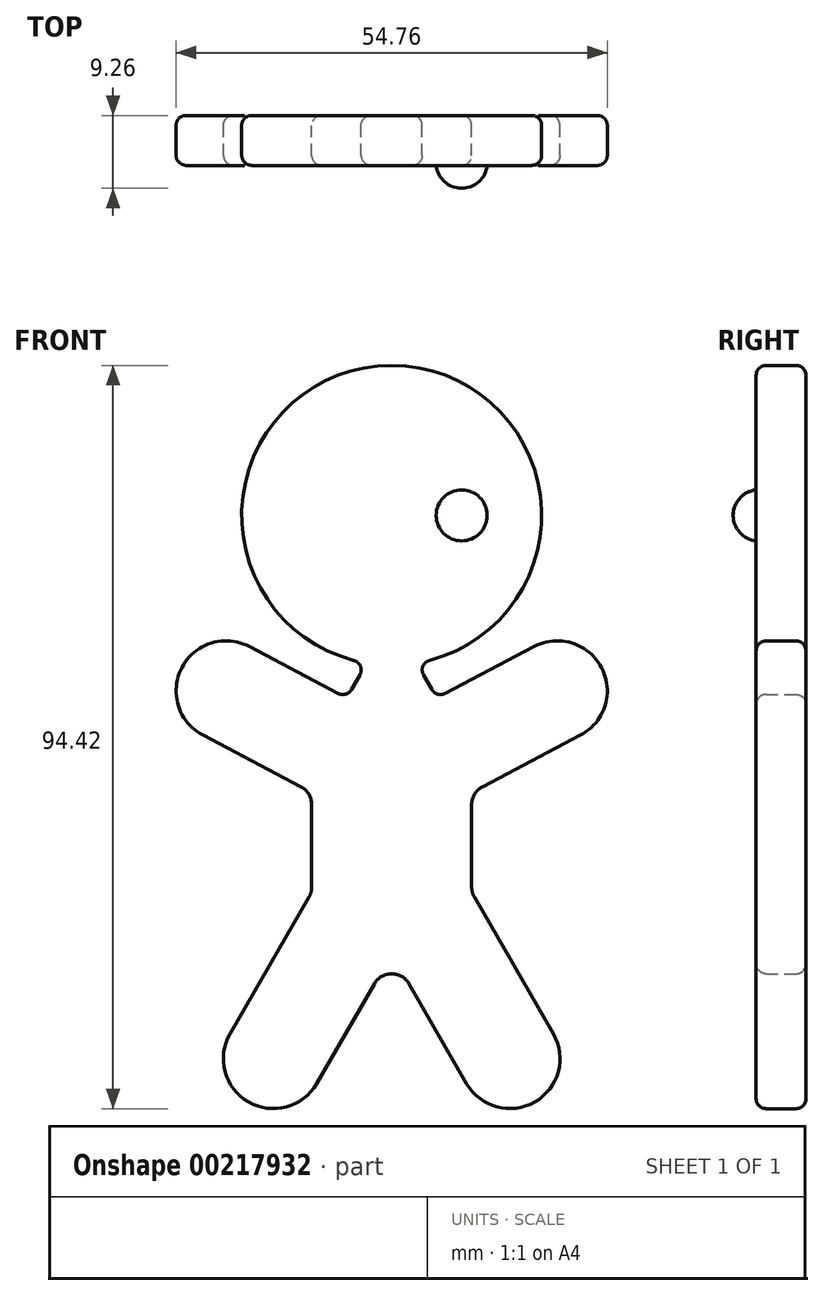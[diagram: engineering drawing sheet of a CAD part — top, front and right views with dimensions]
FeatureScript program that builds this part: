
annotation { "Feature Type Name" : "Feature", "Feature Type Description" : "" }
export const myFeature = defineFeature(function(context is Context, id is Id, definition is map)
    precondition{}
    {
        {
            var Q0;
            Q0=qCreatedBy(makeId("Front.planeOp"),FACE);
            var sketch = newSketch(context, id + "F0", { "sketchPlane" : qUnion([Q0])});
            skArc(sketch, "E0", {"start": v(4.82, 59.27) * mm, "mid": v(0, 96.74) * mm, "end": v(-4.82, 59.27) * mm});
            skLineSegment(sketch, "E1", {"start": v(2.2, 18.19) * mm, "end": v(9.52, 5.5) * mm});
            skLineSegment(sketch, "E2", {"start": v(18.2, 3.18) * mm, "end": v(18.2, 3.18) * mm});
            skLineSegment(sketch, "E3", {"start": v(20.52, 11.85) * mm, "end": v(10.5, 29.21) * mm});
            skLineSegment(sketch, "E4", {"start": v(10.16, 30.48) * mm, "end": v(10.16, 40.97) * mm});
            skLineSegment(sketch, "E5", {"start": v(11.52, 43.21) * mm, "end": v(24, 49.78) * mm});
            skLineSegment(sketch, "E6", {"start": v(26.65, 58.35) * mm, "end": v(26.65, 58.35) * mm});
            skLineSegment(sketch, "E7", {"start": v(18.08, 61.02) * mm, "end": v(6.8, 55.08) * mm});
            skLineSegment(sketch, "E8", {"start": v(0, 77.7) * mm, "end": v(0, 22) * mm, "construction": true});
            skLineSegment(sketch, "E9", {"start": v(5.1, 55.57) * mm, "end": v(4.05, 57.4) * mm});
            skLineSegment(sketch, "E10.MirrorCS", {"start": v(-2.2, 18.19) * mm, "end": v(-9.52, 5.5) * mm});
            skLineSegment(sketch, "E11.MirrorCS", {"start": v(-18.2, 3.17) * mm, "end": v(-18.2, 3.17) * mm});
            skLineSegment(sketch, "E12.MirrorCS", {"start": v(-20.52, 11.85) * mm, "end": v(-10.5, 29.21) * mm});
            skLineSegment(sketch, "E13.MirrorCS", {"start": v(-10.16, 30.48) * mm, "end": v(-10.16, 40.97) * mm});
            skLineSegment(sketch, "E14.MirrorCS", {"start": v(-11.52, 43.21) * mm, "end": v(-24, 49.78) * mm});
            skLineSegment(sketch, "E15.MirrorCS", {"start": v(-26.65, 58.35) * mm, "end": v(-26.65, 58.35) * mm});
            skLineSegment(sketch, "E16.MirrorCS", {"start": v(-18.08, 61.02) * mm, "end": v(-6.8, 55.08) * mm});
            skLineSegment(sketch, "E17.MirrorCS", {"start": v(-5.1, 55.57) * mm, "end": v(-4.05, 57.4) * mm});
            skPoint(sketch, "E18.visualSharp", {"position": v(12.7, 0) * mm});
            skArc(sketch, "E18.filletArc", {"start": v(9.53, 5.5) * mm, "mid": v(13.38, 2.54) * mm, "end": v(18.2, 3.18) * mm});
            skPoint(sketch, "E19.visualSharp", {"position": v(23.7, 6.35) * mm});
            skArc(sketch, "E19.filletArc", {"start": v(18.2, 3.18) * mm, "mid": v(21.16, 7.03) * mm, "end": v(20.52, 11.85) * mm});
            skPoint(sketch, "E20.visualSharp", {"position": v(-12.7, 0) * mm});
            skArc(sketch, "E20.filletArc", {"start": v(-18.2, 3.18) * mm, "mid": v(-13.38, 2.54) * mm, "end": v(-9.52, 5.5) * mm});
            skPoint(sketch, "E21.visualSharp", {"position": v(-23.7, 6.35) * mm});
            skArc(sketch, "E21.filletArc", {"start": v(-20.52, 11.85) * mm, "mid": v(-21.16, 7.03) * mm, "end": v(-18.2, 3.17) * mm});
            skPoint(sketch, "E22.visualSharp", {"position": v(23.7, 63.97) * mm});
            skArc(sketch, "E22.filletArc", {"start": v(26.65, 58.35) * mm, "mid": v(22.92, 61.46) * mm, "end": v(18.08, 61.02) * mm});
            skPoint(sketch, "E23.visualSharp", {"position": v(29.61, 52.73) * mm});
            skArc(sketch, "E23.filletArc", {"start": v(24, 49.78) * mm, "mid": v(27.1, 53.51) * mm, "end": v(26.65, 58.35) * mm});
            skPoint(sketch, "E24.visualSharp", {"position": v(-23.7, 63.97) * mm});
            skArc(sketch, "E24.filletArc", {"start": v(-18.08, 61.02) * mm, "mid": v(-22.92, 61.46) * mm, "end": v(-26.65, 58.35) * mm});
            skPoint(sketch, "E25.visualSharp", {"position": v(-29.61, 52.73) * mm});
            skArc(sketch, "E25.filletArc", {"start": v(-26.65, 58.35) * mm, "mid": v(-27.1, 53.51) * mm, "end": v(-24, 49.78) * mm});
            skPoint(sketch, "E26.visualSharp", {"position": v(0, 22) * mm});
            skArc(sketch, "E26.filletArc", {"start": v(2.2, 18.19) * mm, "mid": v(0, 19.46) * mm, "end": v(-2.2, 18.19) * mm});
            skPoint(sketch, "E27.visualSharp", {"position": v(-10.16, 29.8) * mm});
            skArc(sketch, "E27.filletArc", {"start": v(-10.5, 29.2) * mm, "mid": v(-10.25, 29.82) * mm, "end": v(-10.16, 30.48) * mm});
            skPoint(sketch, "E28.visualSharp", {"position": v(10.16, 29.8) * mm});
            skArc(sketch, "E28.filletArc", {"start": v(10.16, 30.48) * mm, "mid": v(10.25, 29.82) * mm, "end": v(10.5, 29.2) * mm});
            skPoint(sketch, "E29.visualSharp", {"position": v(10.16, 42.5) * mm});
            skArc(sketch, "E29.filletArc", {"start": v(11.52, 43.21) * mm, "mid": v(10.53, 42.28) * mm, "end": v(10.16, 40.97) * mm});
            skPoint(sketch, "E30.visualSharp", {"position": v(-10.16, 42.5) * mm});
            skArc(sketch, "E30.filletArc", {"start": v(-10.16, 40.97) * mm, "mid": v(-10.53, 42.28) * mm, "end": v(-11.52, 43.21) * mm});
            skPoint(sketch, "E31.visualSharp", {"position": v(-5.72, 54.51) * mm});
            skArc(sketch, "E31.filletArc", {"start": v(-6.8, 55.08) * mm, "mid": v(-5.85, 54.98) * mm, "end": v(-5.1, 55.57) * mm});
            skPoint(sketch, "E32.visualSharp", {"position": v(5.72, 54.51) * mm});
            skArc(sketch, "E32.filletArc", {"start": v(5.1, 55.57) * mm, "mid": v(5.85, 54.98) * mm, "end": v(6.8, 55.08) * mm});
            skPoint(sketch, "E33.visualSharp", {"position": v(-3.18, 58.91) * mm});
            skArc(sketch, "E33.filletArc", {"start": v(-4.05, 57.4) * mm, "mid": v(-3.97, 58.53) * mm, "end": v(-4.82, 59.27) * mm});
            skPoint(sketch, "E34.visualSharp", {"position": v(3.18, 58.91) * mm});
            skArc(sketch, "E34.filletArc", {"start": v(4.82, 59.27) * mm, "mid": v(3.97, 58.53) * mm, "end": v(4.05, 57.4) * mm});
            skSolve(sketch);
        }
        {
            var Q0;
            Q0 = qSketchRegion(id + "F0", true);
            extrude(context, id + "F1", {"entities" : qUnion([Q0]), "depth" : 6.35 * mm});
        }
        {
            var Q0;
            Q0=makeQuery(id+"F1.opExtrude","CAP_FACE",FACE,{"disambiguationData":[OSD([sQuery(id+"F0.wireOp",EDGE,"E0"),sQuery(id+"F0.wireOp",EDGE,"E1"),sQuery(id+"F0.wireOp",EDGE,"E3"),sQuery(id+"F0.wireOp",EDGE,"E4"),sQuery(id+"F0.wireOp",EDGE,"E5"),sQuery(id+"F0.wireOp",EDGE,"E7"),sQuery(id+"F0.wireOp",EDGE,"E9"),sQuery(id+"F0.wireOp",EDGE,"E10.MirrorCS"),sQuery(id+"F0.wireOp",EDGE,"E12.MirrorCS"),sQuery(id+"F0.wireOp",EDGE,"E13.MirrorCS"),sQuery(id+"F0.wireOp",EDGE,"E14.MirrorCS"),sQuery(id+"F0.wireOp",EDGE,"E16.MirrorCS"),sQuery(id+"F0.wireOp",EDGE,"E17.MirrorCS"),sQuery(id+"F0.wireOp",EDGE,"E18.filletArc"),sQuery(id+"F0.wireOp",EDGE,"E19.filletArc"),sQuery(id+"F0.wireOp",EDGE,"E20.filletArc"),sQuery(id+"F0.wireOp",EDGE,"E21.filletArc"),sQuery(id+"F0.wireOp",EDGE,"E22.filletArc"),sQuery(id+"F0.wireOp",EDGE,"E23.filletArc"),sQuery(id+"F0.wireOp",EDGE,"E24.filletArc"),sQuery(id+"F0.wireOp",EDGE,"E25.filletArc"),sQuery(id+"F0.wireOp",EDGE,"E26.filletArc"),sQuery(id+"F0.wireOp",EDGE,"E27.filletArc"),sQuery(id+"F0.wireOp",EDGE,"E28.filletArc"),sQuery(id+"F0.wireOp",EDGE,"E29.filletArc"),sQuery(id+"F0.wireOp",EDGE,"E30.filletArc"),sQuery(id+"F0.wireOp",EDGE,"E31.filletArc"),sQuery(id+"F0.wireOp",EDGE,"E32.filletArc"),sQuery(id+"F0.wireOp",EDGE,"E33.filletArc"),sQuery(id+"F0.wireOp",EDGE,"E34.filletArc")])],"isStart":false});
            var Q1;
            Q1=makeQuery(id+"F1.opExtrude","CAP_FACE",FACE,{"disambiguationData":[OSD([sQuery(id+"F0.wireOp",EDGE,"E0"),sQuery(id+"F0.wireOp",EDGE,"E1"),sQuery(id+"F0.wireOp",EDGE,"E3"),sQuery(id+"F0.wireOp",EDGE,"E4"),sQuery(id+"F0.wireOp",EDGE,"E5"),sQuery(id+"F0.wireOp",EDGE,"E7"),sQuery(id+"F0.wireOp",EDGE,"E9"),sQuery(id+"F0.wireOp",EDGE,"E10.MirrorCS"),sQuery(id+"F0.wireOp",EDGE,"E12.MirrorCS"),sQuery(id+"F0.wireOp",EDGE,"E13.MirrorCS"),sQuery(id+"F0.wireOp",EDGE,"E14.MirrorCS"),sQuery(id+"F0.wireOp",EDGE,"E16.MirrorCS"),sQuery(id+"F0.wireOp",EDGE,"E17.MirrorCS"),sQuery(id+"F0.wireOp",EDGE,"E18.filletArc"),sQuery(id+"F0.wireOp",EDGE,"E19.filletArc"),sQuery(id+"F0.wireOp",EDGE,"E20.filletArc"),sQuery(id+"F0.wireOp",EDGE,"E21.filletArc"),sQuery(id+"F0.wireOp",EDGE,"E22.filletArc"),sQuery(id+"F0.wireOp",EDGE,"E23.filletArc"),sQuery(id+"F0.wireOp",EDGE,"E24.filletArc"),sQuery(id+"F0.wireOp",EDGE,"E25.filletArc"),sQuery(id+"F0.wireOp",EDGE,"E26.filletArc"),sQuery(id+"F0.wireOp",EDGE,"E27.filletArc"),sQuery(id+"F0.wireOp",EDGE,"E28.filletArc"),sQuery(id+"F0.wireOp",EDGE,"E29.filletArc"),sQuery(id+"F0.wireOp",EDGE,"E30.filletArc"),sQuery(id+"F0.wireOp",EDGE,"E31.filletArc"),sQuery(id+"F0.wireOp",EDGE,"E32.filletArc"),sQuery(id+"F0.wireOp",EDGE,"E33.filletArc"),sQuery(id+"F0.wireOp",EDGE,"E34.filletArc")])],"isStart":true});
            fillet(context, id + "F2", {"entities" : qUnion([Q0, Q1]), "radius" : 1.27 * mm, "tangentPropagation" : true, "allowEdgeOverflow" : false});
        }
        {
            var Q0;
            Q0=makeQuery(id+"F1.opExtrude","CAP_FACE",FACE,{"disambiguationData":[OSD([sQuery(id+"F0.wireOp",EDGE,"E0"),sQuery(id+"F0.wireOp",EDGE,"E1"),sQuery(id+"F0.wireOp",EDGE,"E3"),sQuery(id+"F0.wireOp",EDGE,"E4"),sQuery(id+"F0.wireOp",EDGE,"E5"),sQuery(id+"F0.wireOp",EDGE,"E7"),sQuery(id+"F0.wireOp",EDGE,"E9"),sQuery(id+"F0.wireOp",EDGE,"E10.MirrorCS"),sQuery(id+"F0.wireOp",EDGE,"E12.MirrorCS"),sQuery(id+"F0.wireOp",EDGE,"E13.MirrorCS"),sQuery(id+"F0.wireOp",EDGE,"E14.MirrorCS"),sQuery(id+"F0.wireOp",EDGE,"E16.MirrorCS"),sQuery(id+"F0.wireOp",EDGE,"E17.MirrorCS"),sQuery(id+"F0.wireOp",EDGE,"E18.filletArc"),sQuery(id+"F0.wireOp",EDGE,"E19.filletArc"),sQuery(id+"F0.wireOp",EDGE,"E20.filletArc"),sQuery(id+"F0.wireOp",EDGE,"E21.filletArc"),sQuery(id+"F0.wireOp",EDGE,"E22.filletArc"),sQuery(id+"F0.wireOp",EDGE,"E23.filletArc"),sQuery(id+"F0.wireOp",EDGE,"E24.filletArc"),sQuery(id+"F0.wireOp",EDGE,"E25.filletArc"),sQuery(id+"F0.wireOp",EDGE,"E26.filletArc"),sQuery(id+"F0.wireOp",EDGE,"E27.filletArc"),sQuery(id+"F0.wireOp",EDGE,"E28.filletArc"),sQuery(id+"F0.wireOp",EDGE,"E29.filletArc"),sQuery(id+"F0.wireOp",EDGE,"E30.filletArc"),sQuery(id+"F0.wireOp",EDGE,"E31.filletArc"),sQuery(id+"F0.wireOp",EDGE,"E32.filletArc"),sQuery(id+"F0.wireOp",EDGE,"E33.filletArc"),sQuery(id+"F0.wireOp",EDGE,"E34.filletArc")])],"isStart":false});
            var sketch = newSketch(context, id + "F3", { "sketchPlane" : qUnion([Q0])});
            skArc(sketch, "E35", {"start": v(8.9, 73.88) * mm, "mid": v(12.7, 77.7) * mm, "end": v(8.9, 81.5) * mm});
            skLineSegment(sketch, "E36", {"start": v(0, 95.47) * mm, "end": v(0, 20.73) * mm, "construction": true});
            skLineSegment(sketch, "E37", {"start": v(8.9, 81.5) * mm, "end": v(8.9, 73.88) * mm, "construction": true});
            skLineSegment(sketch, "E38", {"start": v(8.9, 81.5) * mm, "end": v(8.9, 73.88) * mm});
            skSolve(sketch);
        }
        {
            var Q0;
            Q0=makeQuery(id+"F1.opExtrude","CAP_FACE",FACE,{"disambiguationData":[OSD([sQuery(id+"F0.wireOp",EDGE,"E0"),sQuery(id+"F0.wireOp",EDGE,"E1"),sQuery(id+"F0.wireOp",EDGE,"E3"),sQuery(id+"F0.wireOp",EDGE,"E4"),sQuery(id+"F0.wireOp",EDGE,"E5"),sQuery(id+"F0.wireOp",EDGE,"E7"),sQuery(id+"F0.wireOp",EDGE,"E9"),sQuery(id+"F0.wireOp",EDGE,"E10.MirrorCS"),sQuery(id+"F0.wireOp",EDGE,"E12.MirrorCS"),sQuery(id+"F0.wireOp",EDGE,"E13.MirrorCS"),sQuery(id+"F0.wireOp",EDGE,"E14.MirrorCS"),sQuery(id+"F0.wireOp",EDGE,"E16.MirrorCS"),sQuery(id+"F0.wireOp",EDGE,"E17.MirrorCS"),sQuery(id+"F0.wireOp",EDGE,"E18.filletArc"),sQuery(id+"F0.wireOp",EDGE,"E19.filletArc"),sQuery(id+"F0.wireOp",EDGE,"E20.filletArc"),sQuery(id+"F0.wireOp",EDGE,"E21.filletArc"),sQuery(id+"F0.wireOp",EDGE,"E22.filletArc"),sQuery(id+"F0.wireOp",EDGE,"E23.filletArc"),sQuery(id+"F0.wireOp",EDGE,"E24.filletArc"),sQuery(id+"F0.wireOp",EDGE,"E25.filletArc"),sQuery(id+"F0.wireOp",EDGE,"E26.filletArc"),sQuery(id+"F0.wireOp",EDGE,"E27.filletArc"),sQuery(id+"F0.wireOp",EDGE,"E28.filletArc"),sQuery(id+"F0.wireOp",EDGE,"E29.filletArc"),sQuery(id+"F0.wireOp",EDGE,"E30.filletArc"),sQuery(id+"F0.wireOp",EDGE,"E31.filletArc"),sQuery(id+"F0.wireOp",EDGE,"E32.filletArc"),sQuery(id+"F0.wireOp",EDGE,"E33.filletArc"),sQuery(id+"F0.wireOp",EDGE,"E34.filletArc")])],"isStart":false});
            var sketch = newSketch(context, id + "F4", { "sketchPlane" : qUnion([Q0])});
            skLineSegment(sketch, "E39", {"start": v(0, 95.47) * mm, "end": v(0, 20.73) * mm, "construction": true});
            skFitSpline(sketch, "E40", {"points": [v(0, 68.66) * mm, v(8.71, 69.87) * mm, v(0, 64.67) * mm], "startDerivative": vector(14.82, 0.4) * mm, "endDerivative": vector(-63.33, -2.94) * mm});
            skSolve(sketch);
        }
        {
            var Q0;
            Q0=qCreatedBy(makeId("Right.planeOp"),FACE);
            var sketch = newSketch(context, id + "F5", { "sketchPlane" : qUnion([Q0])});
            skArc(sketch, "E41", {"start": v(-6.35, 69.54) * mm, "mid": v(-7.68, 68.66) * mm, "end": v(-6.35, 67.79) * mm});
            skLineSegment(sketch, "E42", {"start": v(-6.35, 69.54) * mm, "end": v(-6.35, 67.79) * mm});
            skSolve(sketch);
        }
        {
            var Q0;
            Q0=sQuery(id+"F3.wireOp",EDGE,"E38");
            cPlane(context, id + "F6", {"entities" : qUnion([Q0]), "cplaneType" : CPlaneType.LINE_ANGLE, "offset" : 25.4 * mm, "angle" : 0 * degree, "width" : 152.4 * mm, "height" : 152.4 * mm});
        }
        {
            var Q0;
            Q0=qCreatedBy(id+"F6.planeOp",FACE);
            var sketch = newSketch(context, id + "F7", { "sketchPlane" : qUnion([Q0])});
            skLineSegment(sketch, "E43", {"start": v(5.01, 80.8) * mm, "end": v(5.01, 77.7) * mm});
            skLineSegment(sketch, "E44", {"start": v(6, 80.95) * mm, "end": v(6, 74.6) * mm, "construction": true});
            skLineSegment(sketch, "E45", {"start": v(5.01, 77.7) * mm, "end": v(9.26, 77.7) * mm});
            skArc(sketch, "E46.trimOffspring", {"start": v(9.26, 77.7) * mm, "mid": v(7.92, 80.32) * mm, "end": v(5.01, 80.8) * mm});
            skPoint(sketch, "E47.orphan", {"position": v(5.01, 74.6) * mm});
            skLineSegment(sketch, "E48", {"start": v(6.64, 80.89) * mm, "end": v(6.64, 77.7) * mm, "construction": true});
            skSolve(sketch);
        }
        {
            var Q0;
            Q0=makeQuery(id+"F7.imprint","IMPRINT",FACE,{"disambiguationData":[TD([[makeQuery(id+"F7.imprint","IMPRINT",EDGE,{"derivedFrom":sQuery(id+"F7.wireOp",EDGE,"E43")}),1.0]])]});
            var Q1;
            Q1=sQuery(id+"F7.wireOp",EDGE,"E45");
            revolve(context, id + "F8", {"operationType" : NewBodyOperationType.ADD, "entities" : qUnion([Q0]), "axis" : qUnion([Q1]), "revolveType" : RevolveType.FULL});
        }
    });
